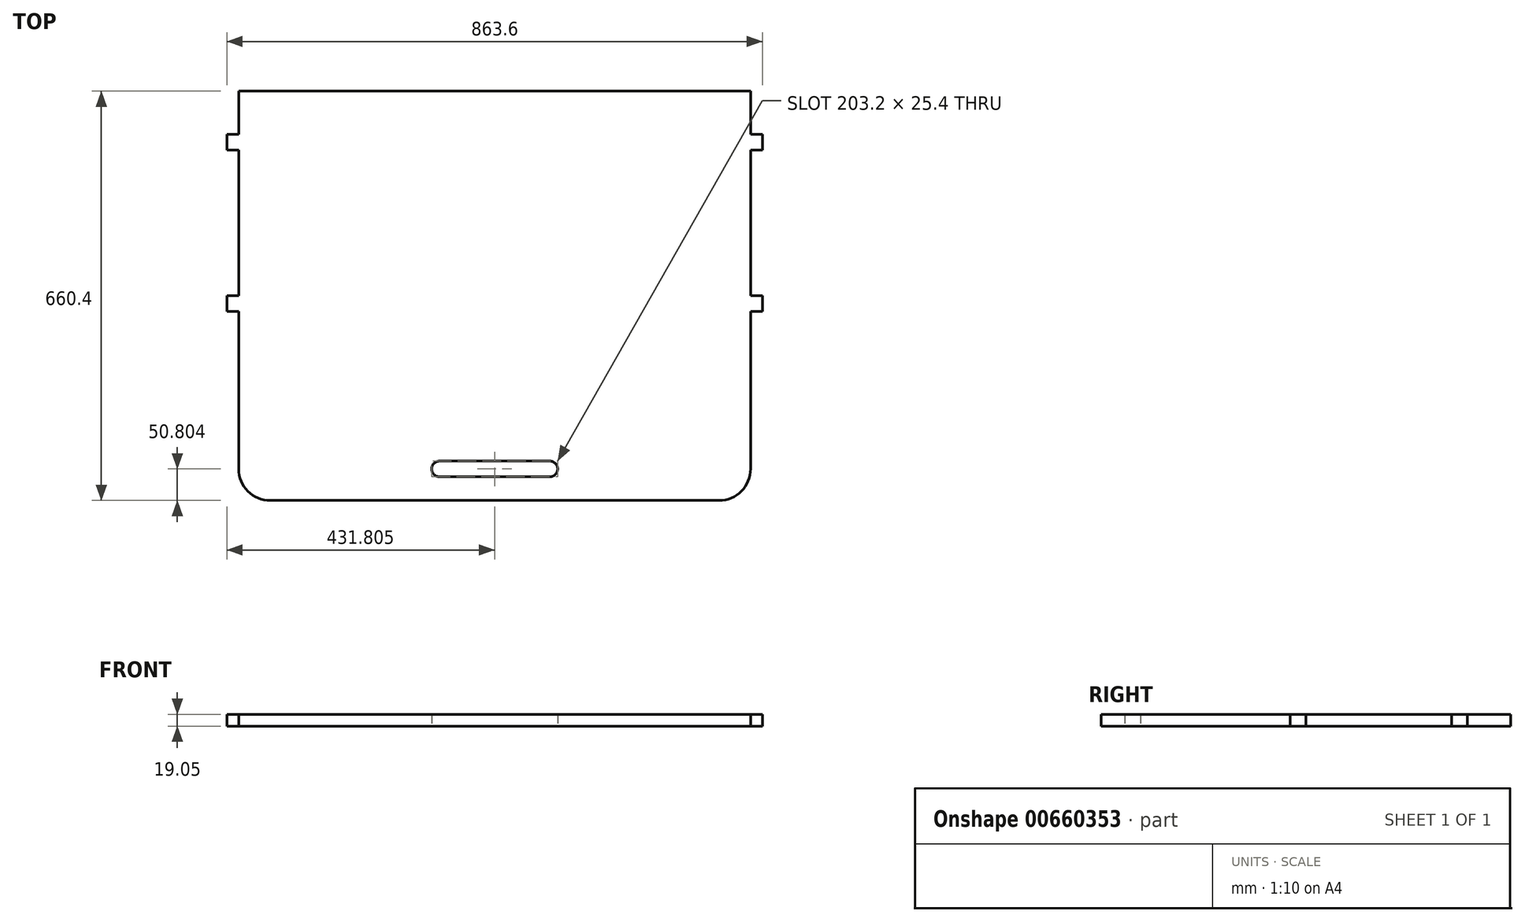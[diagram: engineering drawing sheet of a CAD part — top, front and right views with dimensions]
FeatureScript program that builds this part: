
annotation { "Feature Type Name" : "Feature", "Feature Type Description" : "" }
export const myFeature = defineFeature(function(context is Context, id is Id, definition is map)
    precondition{}
    {
        {
            var Q0;
            Q0=qCreatedBy(makeId("Top.planeOp"),FACE);
            var sketch = newSketch(context, id + "F0", { "sketchPlane" : qUnion([Q0])});
            skLineSegment(sketch, "E0.bottom", {"start": v(-410.74, 224.57) * mm, "end": v(414.76, 224.57) * mm});
            skLineSegment(sketch, "E0.top", {"start": v(-359.94, -435.83) * mm, "end": v(363.96, -435.83) * mm});
            skLineSegment(sketch, "E0.left", {"start": v(-410.74, 224.57) * mm, "end": v(-410.74, -385.03) * mm});
            skLineSegment(sketch, "E0.right", {"start": v(414.76, 224.57) * mm, "end": v(414.76, -385.03) * mm});
            skLineSegment(sketch, "E1.bottom", {"start": v(-410.74, 154.72) * mm, "end": v(-429.79, 154.72) * mm});
            skLineSegment(sketch, "E1.top", {"start": v(-410.74, 129.32) * mm, "end": v(-429.79, 129.32) * mm});
            skLineSegment(sketch, "E1.left", {"start": v(-410.74, 154.72) * mm, "end": v(-410.74, 129.32) * mm});
            skLineSegment(sketch, "E1.right", {"start": v(-429.79, 154.72) * mm, "end": v(-429.79, 129.32) * mm});
            skLineSegment(sketch, "E2.bottom", {"start": v(-410.74, -105.63) * mm, "end": v(-429.79, -105.63) * mm});
            skLineSegment(sketch, "E2.top", {"start": v(-410.74, -131.03) * mm, "end": v(-429.79, -131.03) * mm});
            skLineSegment(sketch, "E2.left", {"start": v(-410.74, -105.63) * mm, "end": v(-410.74, -131.03) * mm});
            skLineSegment(sketch, "E2.right", {"start": v(-429.79, -105.63) * mm, "end": v(-429.79, -131.03) * mm});
            skLineSegment(sketch, "E3.bottom", {"start": v(414.76, 154.72) * mm, "end": v(433.81, 154.72) * mm});
            skLineSegment(sketch, "E3.top", {"start": v(414.76, 129.32) * mm, "end": v(433.81, 129.32) * mm});
            skLineSegment(sketch, "E3.left", {"start": v(414.76, 154.72) * mm, "end": v(414.76, 129.32) * mm});
            skLineSegment(sketch, "E3.right", {"start": v(433.81, 154.72) * mm, "end": v(433.81, 129.32) * mm});
            skLineSegment(sketch, "E4.bottom", {"start": v(414.76, -105.63) * mm, "end": v(433.81, -105.63) * mm});
            skLineSegment(sketch, "E4.top", {"start": v(414.76, -131.03) * mm, "end": v(433.81, -131.03) * mm});
            skLineSegment(sketch, "E4.left", {"start": v(414.76, -105.63) * mm, "end": v(414.76, -131.03) * mm});
            skLineSegment(sketch, "E4.right", {"start": v(433.81, -105.63) * mm, "end": v(433.81, -131.03) * mm});
            skPoint(sketch, "E5.visualSharp", {"position": v(-410.74, -435.83) * mm});
            skArc(sketch, "E5.filletArc", {"start": v(-410.74, -385.03) * mm, "mid": v(-395.86, -420.95) * mm, "end": v(-359.94, -435.83) * mm});
            skPoint(sketch, "E6.visualSharp", {"position": v(414.76, -435.83) * mm});
            skArc(sketch, "E6.filletArc", {"start": v(363.96, -435.83) * mm, "mid": v(399.89, -420.95) * mm, "end": v(414.76, -385.03) * mm});
            skLineSegment(sketch, "E7.bottom", {"start": v(-86.89, -397.73) * mm, "end": v(90.91, -397.73) * mm});
            skLineSegment(sketch, "E7.top", {"start": v(-86.89, -372.33) * mm, "end": v(90.91, -372.33) * mm});
            skLineSegment(sketch, "E7.left", {"start": v(-99.59, -385.03) * mm, "end": v(-99.59, -385.03) * mm});
            skLineSegment(sketch, "E7.right", {"start": v(103.61, -385.03) * mm, "end": v(103.61, -385.03) * mm});
            skPoint(sketch, "E8.visualSharp", {"position": v(103.61, -372.33) * mm});
            skArc(sketch, "E8.filletArc", {"start": v(103.61, -385.03) * mm, "mid": v(99.9, -376.05) * mm, "end": v(90.91, -372.33) * mm});
            skPoint(sketch, "E9.visualSharp", {"position": v(103.61, -397.73) * mm});
            skArc(sketch, "E9.filletArc", {"start": v(90.91, -397.73) * mm, "mid": v(99.9, -394) * mm, "end": v(103.61, -385.03) * mm});
            skPoint(sketch, "E10.visualSharp", {"position": v(-99.59, -372.33) * mm});
            skArc(sketch, "E10.filletArc", {"start": v(-86.89, -372.33) * mm, "mid": v(-95.87, -376.05) * mm, "end": v(-99.59, -385.03) * mm});
            skPoint(sketch, "E11.visualSharp", {"position": v(-99.59, -397.73) * mm});
            skArc(sketch, "E11.filletArc", {"start": v(-99.59, -385.03) * mm, "mid": v(-95.87, -394) * mm, "end": v(-86.89, -397.73) * mm});
            skSolve(sketch);
        }
        {
            var Q0;
            Q0 = qSketchRegion(id + "F0", true);
            extrude(context, id + "F1", {"entities" : qUnion([Q0]), "depth" : 19.05 * mm, "offsetDistance" : 25.4 * mm});
        }
    });
